# Revit family: NBS_GreshamOfficeFurnitureLtd_OffcTbls_ReloTables
name_source: partatom
category: Furniture
units: mm (PartAtom-declared; Revit-internal decimal feet)

## family parameters
Always vertical = Yes
Cut with Voids When Loaded = No
Room Calculation Point = No
Shared = No
Work Plane-Based = No

## types (9) — shared parameters
AssetType = Movable
Category = Pr_40_50_21_60:Office tables
CodePerformance = FSC Certified
Color = Black,White,Grey,Silver
Description = A range of small format tables, available in nine variations for workspace environments
DurationUnit = year
ExposedEdges = Plastics strip
Features = Available in 9 variations, versatile, 20 mm geometric steel frames in four colour options, supplied fully assembled, FSC Certified MFC
Finish = Powder-coated
FrameMaterial = NBS_GreshamOfficeFurnitureLtd_Metal_Black
FrameProfile = 20 mm diameter
FramesColour = White,Grey,Silver,Black
FramesSupports = Mild steel frame, powder-coated
IfcExportAs = IfcFurnitureType
IfcExportType = TABLE
LoadMaximum = 128 kg
ManufacturerName = Gresham Office Furniture Ltd
ManufacturerURL = www.gof.co.uk
Material = MFC,Steel,Acrylonitrile butadiene styrene (ABS)
ModelNumber = RELTA1, RELTA2, RELTB1, RELTB2, RELTC1, RELTC2, RELTC3, RELTD1, RELTD2
NBSCertification = www.nationalbimlibrary.com/cert/cgzjtvqt
Recyclability = 100% recyclable
Shape = Circle,Oval
ShelfMaterial = NBS_GreshamOfficeFurnitureLtd_Beech
Standard = To BS EN 15372, test level 2
StretcherHeight = 202 mm  [stored 0.66273 ft]
SustainabilityPerformance = 100% recyclable,
TableTopMaterial = NBS_GreshamOfficeFurnitureLtd_Beech
Uniclass2015Code = Pr_40_50_21_60
Uniclass2015Title = Office tables
Uniclass2015Version = Products v1.22
Version = 1
WarrantyDescription = Ten year
WarrantyDurationUnit = year
zero-valued in all types: Default Elevation

## per-type parameters (varying)
| type | BIMObjectName | CalcOverallHeight | CalcOverallLength | CalcOverallWidth | DimensionsHeightNominal | DimensionsPlanSize | IsCylindricalTable | IsRELTA | IsRELTB | IsRELTC | IsRELTD | Name | NominalHeight | NominalLength | NominalWidth | ShowRELTBShelf | ShowRELTCShelf | TableTopHeight |
| RELTA1-SmallLowCircularTable | NBS_GreshamOfficeFurnitureLtd_OfficeTables_ReloTables_RELTA1SmallLowCircularTable | 455 mm | 500 mm  [stored 1.64042 ft] | 500 mm  [stored 1.64042 ft] | 455 mm | Ø495 mm | No | Yes | No | No | No | OfficeTables_ReloTables_RELTA1SmallLowCircularTable_GreshamOfficeFurnitureLtd | 455 mm | 500 mm  [stored 1.64042 ft] | 500 mm  [stored 1.64042 ft] | No | No | 455 mm |
| RELTA2-SmallHighCircularTable | NBS_GreshamOfficeFurnitureLtd_OfficeTables_ReloTables_RELTA2SmallHighCircularTable | 575 mm | 500 mm  [stored 1.64042 ft] | 500 mm  [stored 1.64042 ft] | 575 mm | Ø495 mm | No | Yes | No | No | No | OfficeTables_ReloTables_RELTA2SmallHighCircularTable_GreshamOfficeFurnitureLtd | 575 mm | 500 mm  [stored 1.64042 ft] | 500 mm  [stored 1.64042 ft] | No | No | 575 mm |
| RELTB1-LargeCircularTable | NBS_GreshamOfficeFurnitureLtd_OfficeTables_ReloTables_RELTB1LargeCircularTable | 455 mm | 740 mm  [stored 2.42782 ft] | 740 mm  [stored 2.42782 ft] | 455 mm | Ø740 mm | No | No | Yes | No | No | OfficeTables_ReloTables_RELTB1LargeCircularTable_GreshamOfficeFurnitureLtd | 455 mm | 740 mm  [stored 2.42782 ft] | 740 mm  [stored 2.42782 ft] | No | No | 455 mm |
| RELTB2-LargeCircularTableWithShelf | NBS_GreshamOfficeFurnitureLtd_OfficeTables_ReloTables_RELTB2LargeCircularTableWithShelf | 455 mm | 740 mm  [stored 2.42782 ft] | 740 mm  [stored 2.42782 ft] | 455 mm | Ø740 mm | No | No | Yes | No | No | OfficeTables_ReloTables_RELTB2LargeCircularTableWithShelf_GreshamOfficeFurnitureLtd | 455 mm | 740 mm  [stored 2.42782 ft] | 740 mm  [stored 2.42782 ft] | Yes | No | 455 mm |
| RELTC1-LowCylindricalTable | NBS_GreshamOfficeFurnitureLtd_OfficeTables_ReloTables_RELTC1LowCylindricalTable | 455 mm | 500 mm  [stored 1.64042 ft] | 1240 mm  [stored 4.06824 ft] | 455 mm | 1240 x 500 mm | Yes | No | No | Yes | No | OfficeTables_ReloTables_RELTC1LowCylindricalTable_GreshamOfficeFurnitureLtd | 455 mm | 500 mm  [stored 1.64042 ft] | 1240 mm  [stored 4.06824 ft] | No | No | 455 mm |
| RELTC2-HighCylindricalTable | NBS_GreshamOfficeFurnitureLtd_OfficeTables_ReloTables_RELTC2HighCylindricalTable | 575 mm | 500 mm  [stored 1.64042 ft] | 1240 mm  [stored 4.06824 ft] | 575 mm | 1240 x 500 mm | Yes | No | No | Yes | No | OfficeTables_ReloTables_RELTC2HighCylindricalTable_GreshamOfficeFurnitureLtd | 575 mm | 500 mm  [stored 1.64042 ft] | 1240 mm  [stored 4.06824 ft] | No | No | 575 mm |
| RELTC3-HighCylindricalTableWithShelf | NBS_GreshamOfficeFurnitureLtd_OfficeTables_ReloTables_RELTC3HighCylindricalTableWithShelf | 575 mm | 500 mm  [stored 1.64042 ft] | 1240 mm  [stored 4.06824 ft] | 575 mm | 1240 x 500 mm | Yes | No | No | Yes | No | OfficeTables_ReloTables_RELTC3HighCylindricalTableWithShelf_GreshamOfficeFurnitureLtd | 575 mm | 500 mm  [stored 1.64042 ft] | 1240 mm  [stored 4.06824 ft] | No | Yes | 575 mm |
| RELTD1-LowCylindricalTableWithCircularShelf | NBS_GreshamOfficeFurnitureLtd_OfficeTables_ReloTables_RELTD1LowCylindricalTableWithCircularShelf | 570 mm | 500 mm  [stored 1.64042 ft] | 1240 mm  [stored 4.06824 ft] | 455 mm (table); 570 mm (including shelf) | 1240 x 500 mm | Yes | No | No | No | Yes | OfficeTables_ReloTables_RELTD1LowCylindricalTableWithCircularShelf_GreshamOfficeFurnitureLtd | 570 mm | 500 mm  [stored 1.64042 ft] | 1240 mm  [stored 4.06824 ft] | No | No | 455 mm |
| RELTD2-HighCylindricalTableWithCircularShelf | NBS_GreshamOfficeFurnitureLtd_OfficeTables_ReloTables_RELTD2HighCylindricalTableWithCircularShelf | 690 mm | 500 mm  [stored 1.64042 ft] | 1240 mm  [stored 4.06824 ft] | 575 mm (table); 690 mm (including shelf) | 1240 x 500 mm | Yes | No | No | No | Yes | OfficeTables_ReloTables_RELTD2HighCylindricalTableWithCircularShelf_GreshamOfficeFurnitureLtd | 690 mm | 500 mm  [stored 1.64042 ft] | 1240 mm  [stored 4.06824 ft] | No | No | 575 mm |

note: column(s) folded — value = type name in every type: ModelReference

note: [stored X ft] marks values corroborated as IEEE doubles in the binary element streams (Revit-internal decimal feet)

## geometry (parser evidence)
native form markers: Sweep x3
no freeform markers — native parametric forms only
